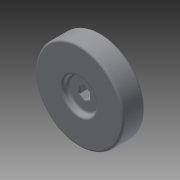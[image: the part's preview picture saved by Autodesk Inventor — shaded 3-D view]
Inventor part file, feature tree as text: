
AUTODESK INVENTOR PART (.ipt)
format: ipt  version: 2015 (Build 190159000, 159)  size: 152,576 bytes
history: native  units: in
note: dims shown in document units (in); Inventor stores cm internally (conversion verified against a paired STEP export)
features: extrude x3, fillet x3, sketch x3
ambient origin geometry x8: Origin, YZ Plane, XZ Plane, XY Plane, X Axis, Y Axis, Z Axis, Center Point
bodies: Solid1 (feature_tree)
feature tree (9):
  extrude  "Extrusion1"  Depth=0.5in TaperAngle=0.0deg
  extrude  "Extrusion2"  Depth=0.5in TaperAngle=0.0deg
  extrude  "Extrusion3"  Depth=0.125in TaperAngle=0.0deg
  fillet  "Fillet1"  Radius=0.03in
  fillet  "Fillet2"  Radius=0.03in
  fillet  "Fillet3"  Radius=0.05in
  sketch  "Sketch1"  dims[d0=2.0in d1=0.5in d2=0.0in]
  sketch  "Sketch2"  dims[d3=0.1254in d4=0.5in d5=0.0in]
  sketch  "Sketch3"  dims[d6=0.75in d7=0.125in d8=0.0in d9=0.03in d10=0.03in d11=0.05in]
